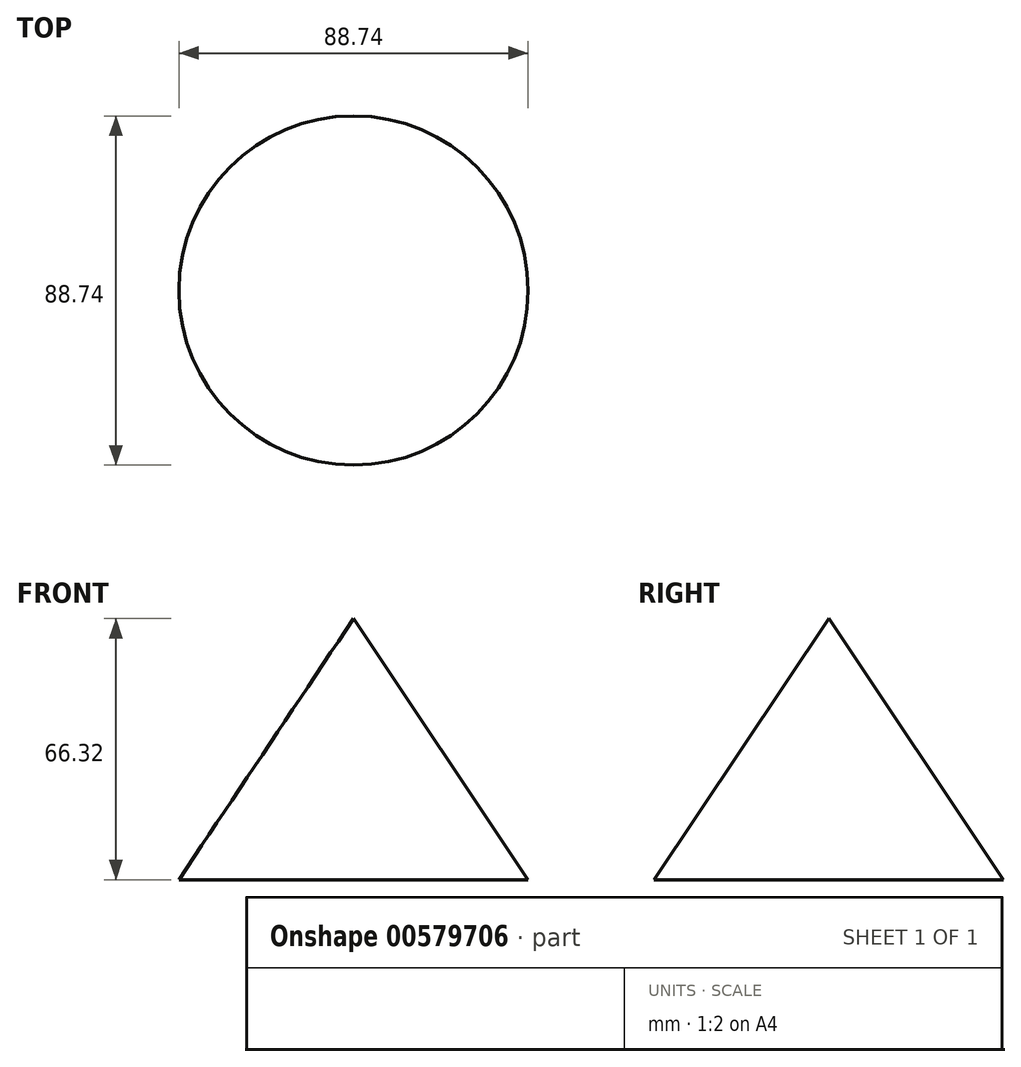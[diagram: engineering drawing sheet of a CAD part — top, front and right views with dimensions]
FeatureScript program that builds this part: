
annotation { "Feature Type Name" : "Feature", "Feature Type Description" : "" }
export const myFeature = defineFeature(function(context is Context, id is Id, definition is map)
    precondition{}
    {
        {
            var Q0;
            Q0=qCreatedBy(makeId("Front.planeOp"),FACE);
            var sketch = newSketch(context, id + "F0", { "sketchPlane" : qUnion([Q0])});
            skLineSegment(sketch, "E0", {"start": v(0, 0) * mm, "end": v(0, 66.32) * mm});
            skLineSegment(sketch, "E1", {"start": v(0, 66.32) * mm, "end": v(44.37, 0) * mm});
            skLineSegment(sketch, "E2", {"start": v(44.37, 0) * mm, "end": v(0, 0) * mm});
            skSolve(sketch);
        }
        {
            var Q0;
            Q0=makeQuery(id+"F0.imprint","IMPRINT",FACE,{"disambiguationData":[TD([[makeQuery(id+"F0.imprint","IMPRINT",EDGE,{"derivedFrom":sQuery(id+"F0.wireOp",EDGE,"E0")}),-1.0]])]});
            var Q1;
            Q1=sQuery(id+"F0.wireOp",EDGE,"E0");
            revolve(context, id + "F1", {"entities" : qUnion([Q0]), "axis" : qUnion([Q1]), "revolveType" : RevolveType.FULL});
        }
    });
